# Revit family: IS_Contour21_S2664_BIM_BE
name_source: partatom
category: Plumbing Fixtures
revit_build: Autodesk Revit 2015 (Build: 20140606_1530(x64)
units: mm (PartAtom-declared; Revit-internal decimal feet)

## types (1)
- S2664MA - Contour 21 Lavabo 60cm 1KG sans trop-plein
    BimObjectNaam = Lavabo__S266401
    Breedte = 0
    BrutoGewicht = 0
    Cost = 0 $
    Default Elevation = 845 mm
    Diepte = 0 mm  [stored 0 ft]
    Dimensions = 414 x 599 x 180 mm
    DuurEenheid = jaar
    GrootteAfvoergat = 0
    Hauteur = 180 mm
    IfcExportAs = IfcSanitaryTerminalType
    IfcExportType = WASHHANDBASINS
    Largeur = 599 mm
    Lengte = 0 mm  [stored 0 ft]
    Longueur = 414 mm
    Manufacturer = www.idealstandard.be
    Model = S266401
    Nettogewicht = 0
    URL = www.idealstandard.be
    Uniclass2015Beschrijving = Wash basins, sinks and troughs
    Uniclass2015Referentie = Pr_40_20_96
    Uniclass2015Version = Products v1.1
    Urlproducent = www.idealstandard.be
    Versie = 1
    Vervangingskosten = 0
    Volumeunits = liter

note: [stored X ft] marks values corroborated as IEEE doubles in the binary element streams (Revit-internal decimal feet)

## geometry (parser evidence)
native form markers: Blend x4, Sweep x1
no freeform markers — native parametric forms only
